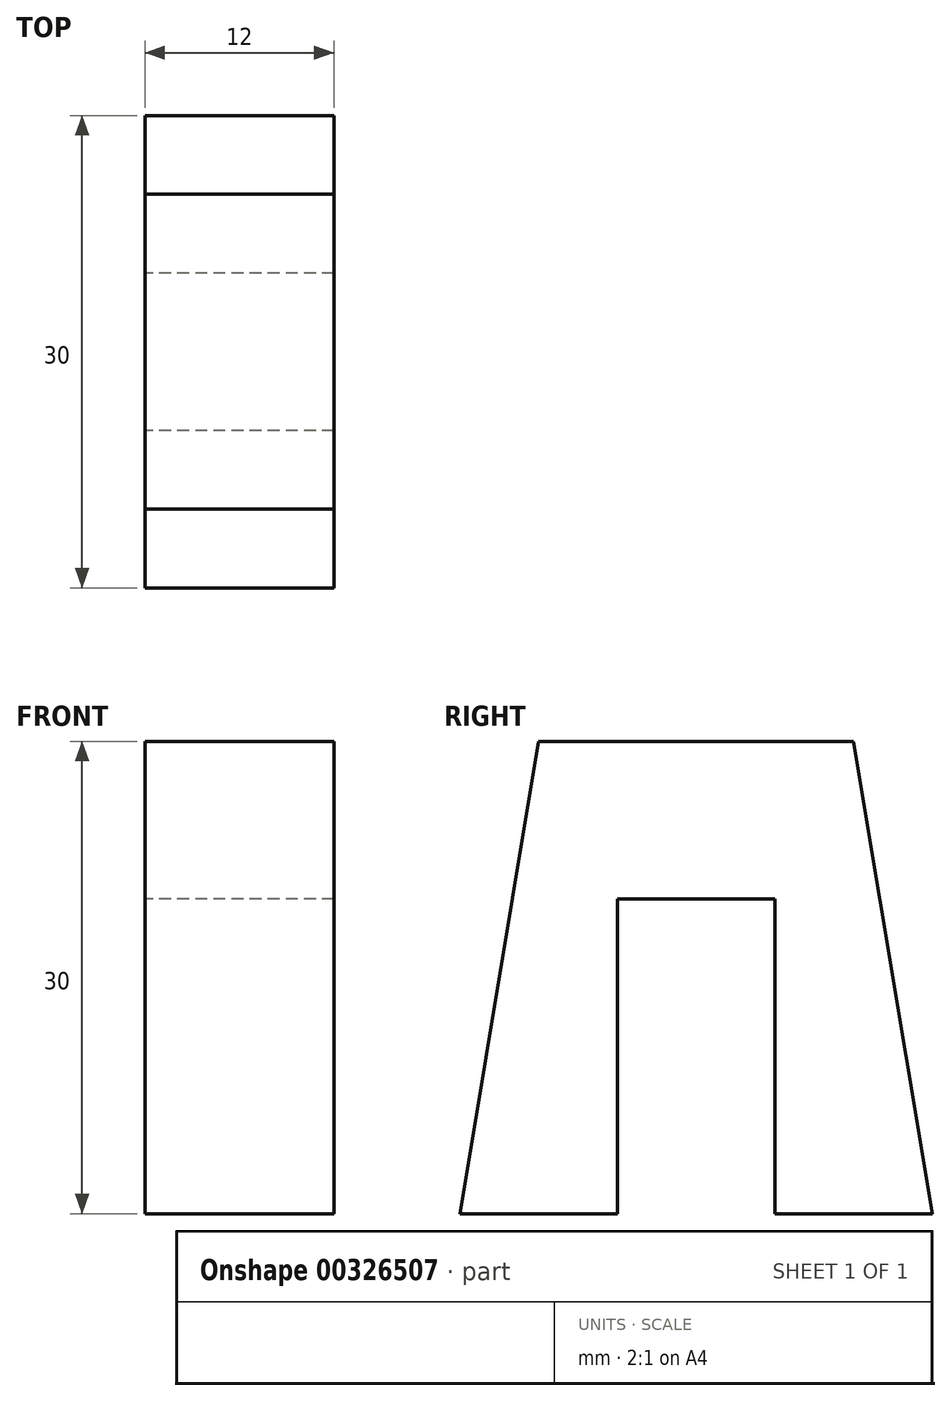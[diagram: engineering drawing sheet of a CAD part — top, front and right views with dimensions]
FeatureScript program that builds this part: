
annotation { "Feature Type Name" : "Feature", "Feature Type Description" : "" }
export const myFeature = defineFeature(function(context is Context, id is Id, definition is map)
    precondition{}
    {
        {
            var Q0;
            Q0=qCreatedBy(makeId("Right.planeOp"),FACE);
            var sketch = newSketch(context, id + "F0", { "sketchPlane" : qUnion([Q0])});
            skLineSegment(sketch, "E0", {"start": v(0, 0) * mm, "end": v(10, 0) * mm});
            skLineSegment(sketch, "E1", {"start": v(25, 30) * mm, "end": v(5, 30) * mm});
            skLineSegment(sketch, "E2", {"start": v(5, 30) * mm, "end": v(25, 30) * mm, "construction": true});
            skLineSegment(sketch, "E3", {"start": v(25, 30) * mm, "end": v(30, 0) * mm});
            skLineSegment(sketch, "E4", {"start": v(5, 30) * mm, "end": v(0, 0) * mm});
            skLineSegment(sketch, "E5", {"start": v(0, 0) * mm, "end": v(10, 0) * mm, "construction": true});
            skLineSegment(sketch, "E6", {"start": v(10, 0) * mm, "end": v(10, 20) * mm});
            skLineSegment(sketch, "E7", {"start": v(10, 20) * mm, "end": v(20, 20) * mm});
            skLineSegment(sketch, "E8", {"start": v(20, 20) * mm, "end": v(20, 0) * mm});
            skPoint(sketch, "E9.orphan", {"position": v(0, 30) * mm});
            skLineSegment(sketch, "E10.trimOffspring", {"start": v(20, 0) * mm, "end": v(30, 0) * mm});
            skSolve(sketch);
        }
        {
            var Q0;
            Q0=makeQuery(id+"F0.imprint","IMPRINT",FACE,{"disambiguationData":[TD([[makeQuery(id+"F0.imprint","IMPRINT",EDGE,{"derivedFrom":sQuery(id+"F0.wireOp",EDGE,"E0")}),1.0]])]});
            extrude(context, id + "F1", {"entities" : qUnion([Q0]), "depth" : 12 * mm});
        }
    });
